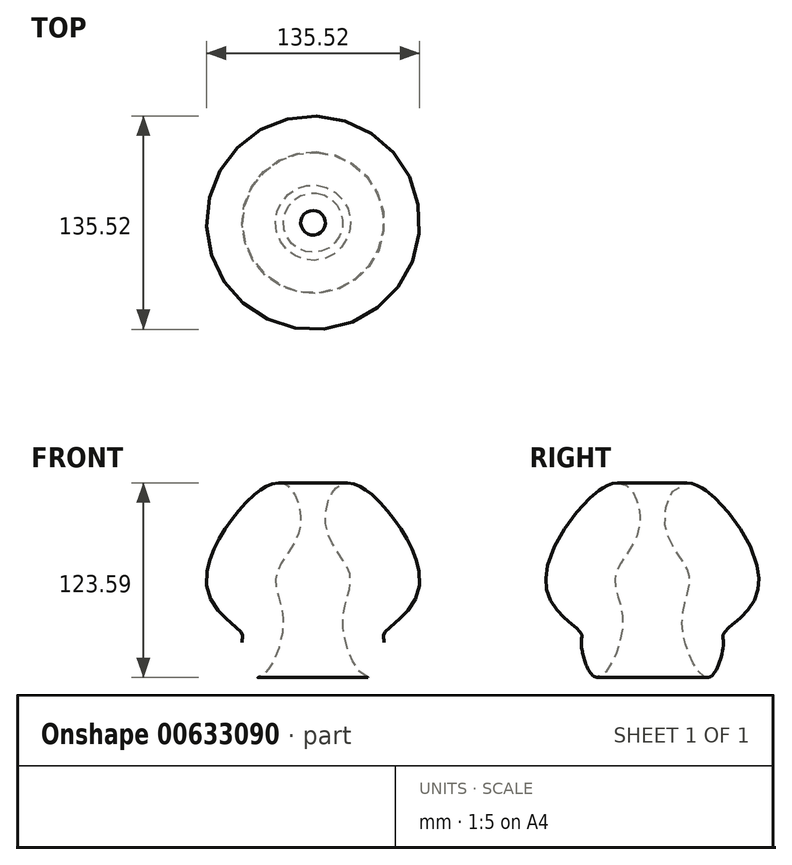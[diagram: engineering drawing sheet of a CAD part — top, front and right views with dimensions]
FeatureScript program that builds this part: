
annotation { "Feature Type Name" : "Feature", "Feature Type Description" : "" }
export const myFeature = defineFeature(function(context is Context, id is Id, definition is map)
    precondition{}
    {
        {
            var Q0;
            Q0=qCreatedBy(makeId("Top.planeOp"),FACE);
            var sketch = newSketch(context, id + "F0", { "sketchPlane" : qUnion([Q0])});
            skCircle(sketch, "E0", {"center": v(-2.22, 0) * mm, "radius": 50 * mm});
            skSolve(sketch);
        }
        {
            var Q0;
            Q0=qCreatedBy(makeId("Right.planeOp"),FACE);
            var sketch = newSketch(context, id + "F1", { "sketchPlane" : qUnion([Q0])});
            skFitSpline(sketch, "E1", {"points": [v(45.1, -33.87) * mm, v(45.1, -28.25) * mm, v(63.45, -9.32) * mm, v(60.79, 29.73) * mm, v(19.97, 67.3) * mm, v(8.13, 38.6) * mm, v(23.52, 8.43) * mm, v(18.78, -22.33) * mm, v(35.64, -56.05) * mm, v(45.1, -33.87) * mm]});
            skSolve(sketch);
        }
        {
            var Q0;
            Q0=makeQuery(id+"F1.imprint","IMPRINT",FACE,{"disambiguationData":[TD([[makeQuery(id+"F1.imprint","IMPRINT",EDGE,{"derivedFrom":sQuery(id+"F1.wireOp",EDGE,"E1")}),1.0]])]});
            var Q1;
            Q1=sQuery(id+"F0.wireOp",EDGE,"E0");
            revolve(context, id + "F2", {"entities" : qUnion([Q0]), "axis" : qUnion([Q1]), "revolveType" : RevolveType.FULL});
        }
    });
